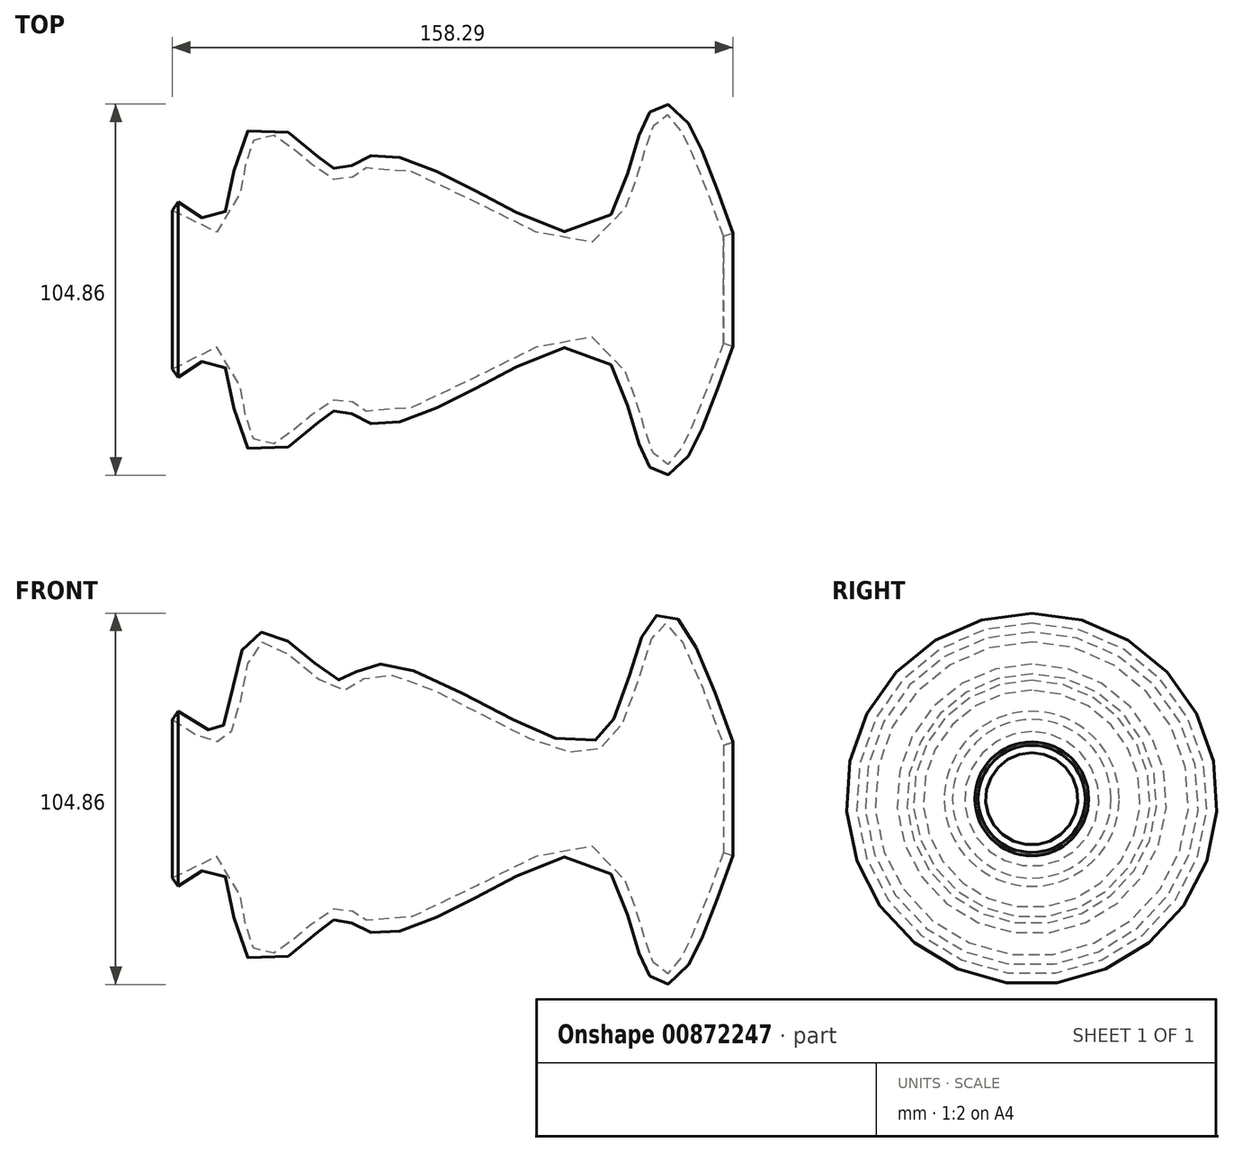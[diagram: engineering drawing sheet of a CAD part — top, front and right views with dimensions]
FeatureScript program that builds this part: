
annotation { "Feature Type Name" : "Feature", "Feature Type Description" : "" }
export const myFeature = defineFeature(function(context is Context, id is Id, definition is map)
    precondition{}
    {
        {
            var Q0;
            Q0=qCreatedBy(makeId("Front.planeOp"),FACE);
            var sketch = newSketch(context, id + "F0", { "sketchPlane" : qUnion([Q0])});
            skLineSegment(sketch, "E0", {"start": v(-89.86, 0) * mm, "end": v(0, 0) * mm, "construction": true});
            skFitSpline(sketch, "E1", {"points": [v(-70.9, 22.42) * mm, v(-58.5, 16.22) * mm, v(-52.67, 23.15) * mm, v(-45.38, 44.29) * mm, v(-24.24, 30.8) * mm, v(-13.67, 35.18) * mm, v(31.9, 16.22) * mm, v(54.5, 18.4) * mm, v(67.25, 49.4) * mm, v(84.75, 15.13) * mm], "startDerivative": vector(159.55, -110.94) * mm, "endDerivative": vector(137.04, -386.16) * mm});
            skFitSpline(sketch, "E2.0", {"points": [v(-69.3, 24.71) * mm, v(-68.47, 24.13) * mm, v(-66.83, 23) * mm, v(-64.47, 21.44) * mm, v(-62.29, 20.17) * mm, v(-60.7, 19.46) * mm, v(-59.66, 19.14) * mm, v(-59.12, 19.04) * mm, v(-58.78, 19.01) * mm, v(-58.5, 19.01) * mm, v(-58.22, 19.06) * mm, v(-57.95, 19.15) * mm, v(-57.67, 19.32) * mm, v(-57.33, 19.62) * mm, v(-56.8, 20.26) * mm, v(-56.22, 21.34) * mm, v(-55.66, 22.86) * mm, v(-55.14, 24.66) * mm, v(-54.54, 27.5) * mm, v(-53.88, 31.4) * mm, v(-53.28, 34.76) * mm, v(-52.7, 37.38) * mm, v(-52.22, 39.27) * mm, v(-51.64, 41.06) * mm, v(-50.93, 42.74) * mm, v(-50.04, 44.3) * mm, v(-49.03, 45.46) * mm, v(-48, 46.25) * mm, v(-47.1, 46.72) * mm, v(-46.25, 46.98) * mm, v(-45.55, 47.1) * mm, v(-44.87, 47.14) * mm, v(-44.04, 47.09) * mm, v(-42.8, 46.84) * mm, v(-41.35, 46.3) * mm, v(-39.7, 45.4) * mm, v(-38.08, 44.32) * mm, v(-36.45, 43.1) * mm, v(-34.83, 41.8) * mm, v(-33.2, 40.43) * mm, v(-31.6, 39.06) * mm, v(-30.03, 37.73) * mm, v(-28.52, 36.5) * mm, v(-27.09, 35.4) * mm, v(-25.78, 34.51) * mm, v(-24.83, 33.98) * mm, v(-24.2, 33.7) * mm, v(-23.87, 33.6) * mm, v(-23.67, 33.54) * mm, v(-23.5, 33.5) * mm, v(-23.23, 33.47) * mm, v(-22.93, 33.5) * mm, v(-22.48, 33.63) * mm, v(-21.86, 33.95) * mm, v(-21.08, 34.46) * mm, v(-20.15, 35.12) * mm, v(-19.08, 35.88) * mm, v(-17.81, 36.66) * mm, v(-16.58, 37.25) * mm, v(-15.47, 37.63) * mm, v(-14.58, 37.86) * mm, v(-13.64, 38.02) * mm, v(-12.68, 38.1) * mm, v(-11.72, 38.1) * mm, v(-10.41, 38.04) * mm, v(-8.75, 37.81) * mm, v(-6.69, 37.36) * mm, v(-4.56, 36.74) * mm, v(-1.63, 35.72) * mm, v(2.2, 34.14) * mm, v(7, 31.88) * mm, v(11.94, 29.37) * mm, v(16.93, 26.75) * mm, v(21.87, 24.14) * mm, v(26.67, 21.69) * mm, v(30.47, 19.88) * mm, v(33.33, 18.64) * mm, v(36.05, 17.56) * mm, v(39.18, 16.52) * mm, v(42.49, 15.84) * mm, v(45.3, 15.74) * mm, v(47.6, 16.2) * mm, v(49.27, 17.02) * mm, v(50.53, 18.03) * mm, v(51.3, 18.84) * mm, v(51.92, 19.6) * mm, v(52.52, 20.45) * mm, v(53.27, 21.68) * mm, v(54.14, 23.4) * mm, v(55.27, 25.96) * mm, v(56.57, 29.55) * mm, v(58.01, 34.14) * mm, v(59.14, 37.96) * mm, v(60.02, 40.86) * mm, v(60.68, 42.94) * mm, v(61.35, 44.89) * mm, v(62.05, 46.67) * mm, v(62.8, 48.3) * mm, v(63.5, 49.5) * mm, v(64.16, 50.38) * mm, v(64.74, 51.01) * mm, v(65.32, 51.5) * mm, v(65.87, 51.83) * mm, v(66.48, 52.12) * mm, v(67.31, 52.37) * mm, v(68.35, 52.42) * mm, v(69.33, 52.24) * mm, v(70.18, 51.91) * mm, v(70.93, 51.48) * mm, v(71.82, 50.81) * mm, v(72.79, 49.84) * mm, v(73.85, 48.47) * mm, v(74.87, 46.9) * mm, v(75.88, 45.1) * mm, v(76.88, 43.13) * mm, v(77.9, 40.97) * mm, v(79.26, 37.85) * mm, v(81, 33.58) * mm, v(83.1, 28) * mm, v(85.24, 22.1) * mm, v(86.67, 18.07) * mm, v(87.39, 16.06) * mm]});
            skLineSegment(sketch, "E3", {"start": v(-70.9, 22.42) * mm, "end": v(-69.3, 24.71) * mm});
            skLineSegment(sketch, "E4", {"start": v(84.75, 15.13) * mm, "end": v(87.39, 16.06) * mm});
            skSolve(sketch);
        }
        {
            var Q0;
            Q0=makeQuery(id+"F0.imprint","IMPRINT",FACE,{"disambiguationData":[TD([[makeQuery(id+"F0.imprint","IMPRINT",EDGE,{"derivedFrom":sQuery(id+"F0.wireOp",EDGE,"E1")}),1.0]])]});
            var Q1;
            Q1=sQuery(id+"F0.wireOp",EDGE,"E0");
            revolve(context, id + "F1", {"surfaceOperationType" : NewSurfaceOperationType.NEW, "entities" : qUnion([Q0]), "axis" : qUnion([Q1]), "revolveType" : RevolveType.FULL});
        }
    });
